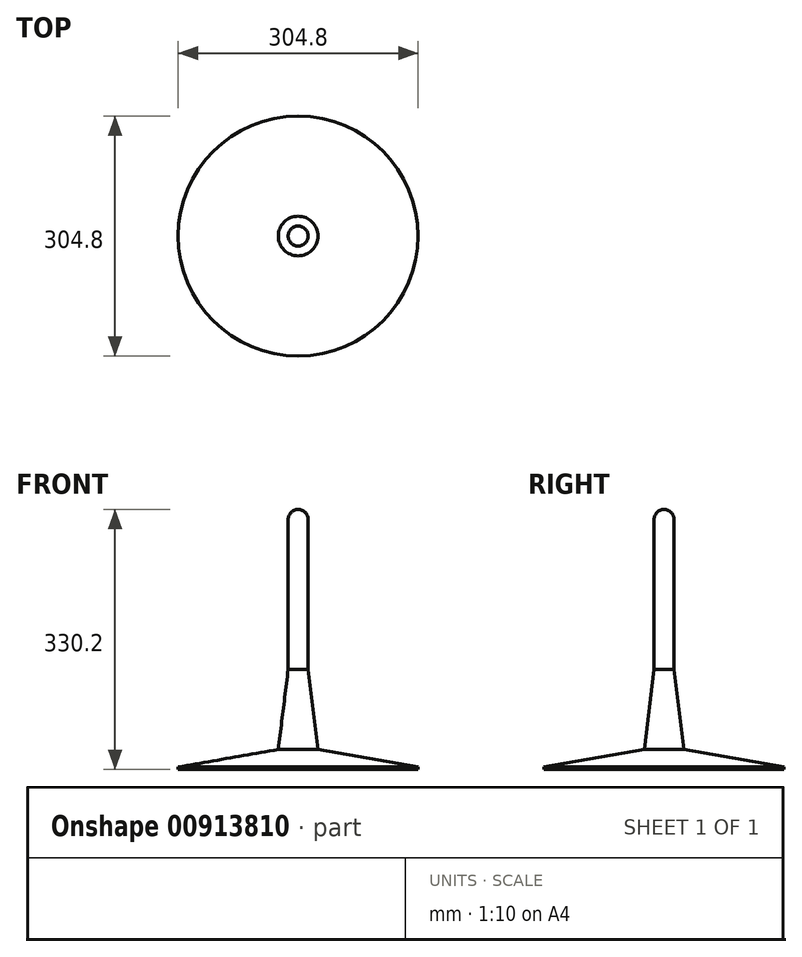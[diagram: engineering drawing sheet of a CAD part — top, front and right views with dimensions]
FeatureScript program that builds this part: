
annotation { "Feature Type Name" : "Feature", "Feature Type Description" : "" }
export const myFeature = defineFeature(function(context is Context, id is Id, definition is map)
    precondition{}
    {
        {
            var Q0;
            Q0=qCreatedBy(makeId("Top.planeOp"),FACE);
            var sketch = newSketch(context, id + "F0", { "sketchPlane" : qUnion([Q0])});
            skCircle(sketch, "E0", {"center": v(0, 0) * mm, "radius": 152.4 * mm});
            skSolve(sketch);
        }
        {
            var Q0;
            Q0 = qSketchRegion(id + "F0", true);
            extrude(context, id + "F1", {"entities" : qUnion([Q0]), "depth" : 25.4 * mm, "offsetDistance" : 25.4 * mm});
        }
        {
            var Q0;
            Q0=makeQuery(id+"F1.opExtrude","CAP_EDGE",EDGE,{"disambiguationData":[OSD([sQuery(id+"F0.wireOp",EDGE,"E0")])],"isStart":false});
            chamfer(context, id + "F2", {"entities" : qUnion([Q0]), "chamferType" : ChamferType.OFFSET_ANGLE, "width" : 127 * mm, "oppositeDirection" : false, "angle" : 10 * degree, "tangentPropagation" : true});
        }
        {
            var Q0;
            Q0=makeQuery(id+"F1.opExtrude","CAP_FACE",FACE,{"disambiguationData":[OSD([sQuery(id+"F0.wireOp",EDGE,"E0")])],"isStart":false});
            var sketch = newSketch(context, id + "F3", { "sketchPlane" : qUnion([Q0])});
            skCircle(sketch, "E1", {"center": v(0, 0) * mm, "radius": 25.4 * mm});
            skSolve(sketch);
        }
        {
            var Q0;
            Q0 = qSketchRegion(id + "F3", true);
            extrude(context, id + "F4", {"entities" : qUnion([Q0]), "operationType" : NewBodyOperationType.ADD, "depth" : 101.6 * mm, "offsetDistance" : 25.4 * mm});
        }
        {
            var Q0;
            Q0=makeQuery(id+"F4.opExtrude","CAP_EDGE",EDGE,{"disambiguationData":[OSD([sQuery(id+"F3.wireOp",EDGE,"E1")])],"isStart":false});
            chamfer(context, id + "F5", {"entities" : qUnion([Q0]), "chamferType" : ChamferType.OFFSET_ANGLE, "width" : 12.7 * mm, "oppositeDirection" : false, "angle" : 83 * degree, "tangentPropagation" : true});
        }
        {
            var Q0;
            Q0=makeQuery(id+"F4.opExtrude","CAP_FACE",FACE,{"disambiguationData":[OSD([sQuery(id+"F3.wireOp",EDGE,"E1")])],"isStart":false});
            var sketch = newSketch(context, id + "F6", { "sketchPlane" : qUnion([Q0])});
            skCircle(sketch, "E2", {"center": v(0, 0) * mm, "radius": 12.7 * mm});
            skSolve(sketch);
        }
        {
            var Q0;
            Q0 = qSketchRegion(id + "F6", true);
            extrude(context, id + "F7", {"entities" : qUnion([Q0]), "operationType" : NewBodyOperationType.ADD, "depth" : 203.2 * mm, "offsetDistance" : 25.4 * mm});
        }
        {
            var Q0;
            Q0=makeQuery(id+"F7.opExtrude","CAP_EDGE",EDGE,{"disambiguationData":[OSD([sQuery(id+"F6.wireOp",EDGE,"E2")])],"isStart":false});
            fillet(context, id + "F8", {"entities" : qUnion([Q0]), "radius" : 12.7 * mm, "tangentPropagation" : true, "allowEdgeOverflow" : false});
        }
    });
